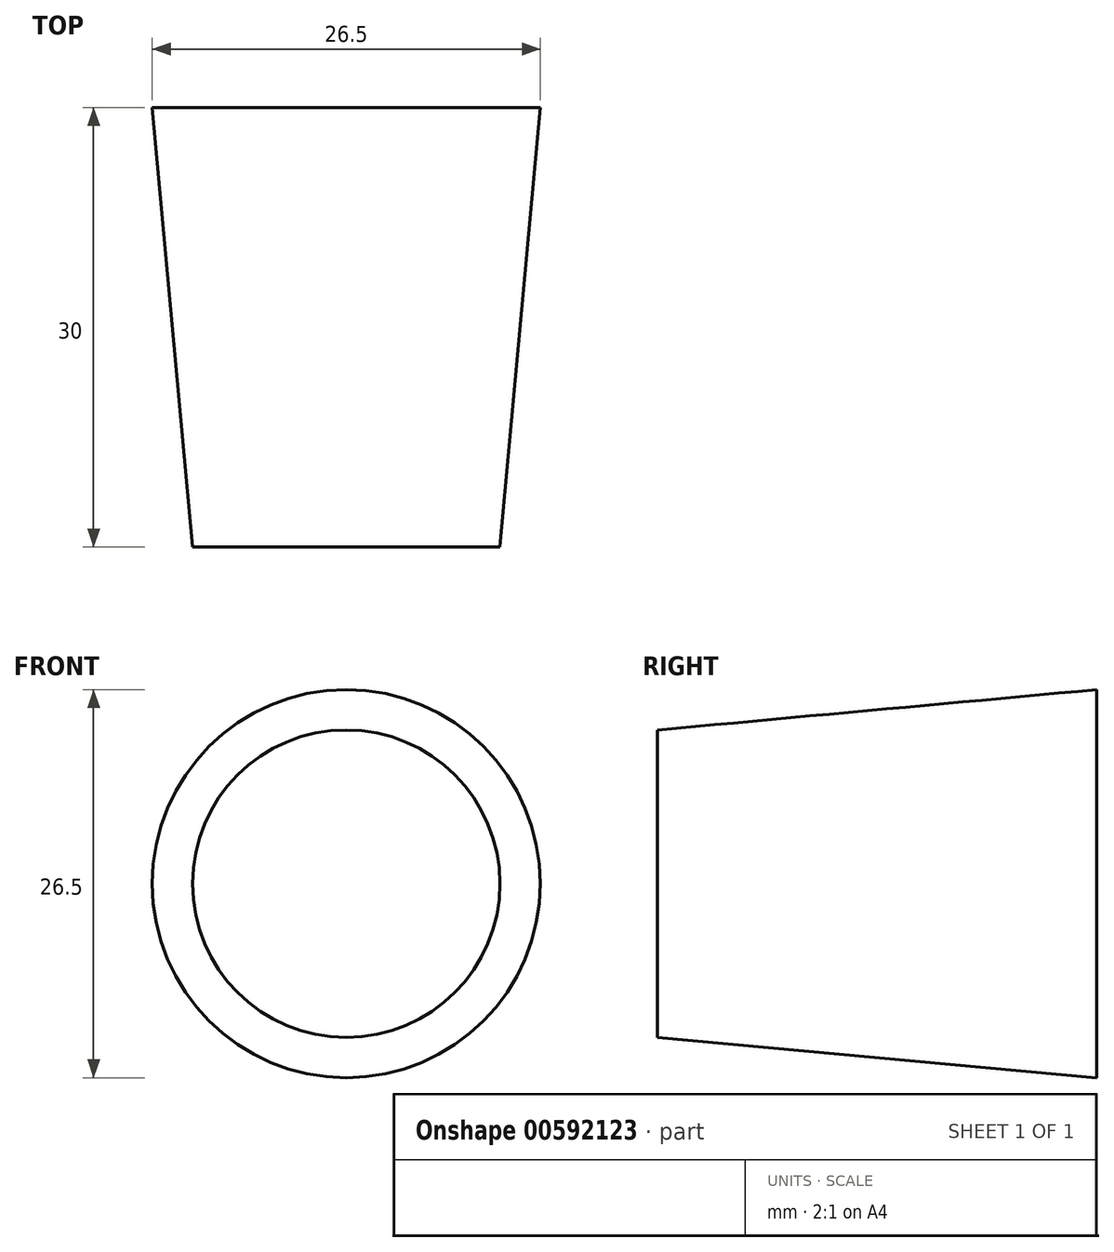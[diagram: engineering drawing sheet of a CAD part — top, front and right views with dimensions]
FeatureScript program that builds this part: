
annotation { "Feature Type Name" : "Feature", "Feature Type Description" : "" }
export const myFeature = defineFeature(function(context is Context, id is Id, definition is map)
    precondition{}
    {
        {
            var Q0;
            Q0=qCreatedBy(makeId("Top.planeOp"),FACE);
            var sketch = newSketch(context, id + "F0", { "sketchPlane" : qUnion([Q0])});
            skLineSegment(sketch, "E0", {"start": v(0, 0) * mm, "end": v(10.5, 0) * mm});
            skLineSegment(sketch, "E1", {"start": v(10.5, 0) * mm, "end": v(13.25, 30) * mm});
            skLineSegment(sketch, "E2", {"start": v(-13.25, 30) * mm, "end": v(-10.5, 0) * mm, "construction": true});
            skLineSegment(sketch, "E3", {"start": v(-10.5, 0) * mm, "end": v(0, 0) * mm, "construction": true});
            skLineSegment(sketch, "E4", {"start": v(-13.25, 30) * mm, "end": v(0, 30) * mm, "construction": true});
            skLineSegment(sketch, "E5", {"start": v(0, 30) * mm, "end": v(13.25, 30) * mm});
            skLineSegment(sketch, "E6", {"start": v(0, 30) * mm, "end": v(0, 0) * mm});
            skSolve(sketch);
        }
        {
            var Q0;
            Q0=makeQuery(id+"F0.imprint","IMPRINT",FACE,{"disambiguationData":[TD([[makeQuery(id+"F0.imprint","IMPRINT",EDGE,{"derivedFrom":sQuery(id+"F0.wireOp",EDGE,"E0")}),1.0]])]});
            var Q1;
            Q1=sQuery(id+"F0.wireOp",EDGE,"E6");
            revolve(context, id + "F1", {"entities" : qUnion([Q0]), "axis" : qUnion([Q1]), "revolveType" : RevolveType.FULL});
        }
    });
